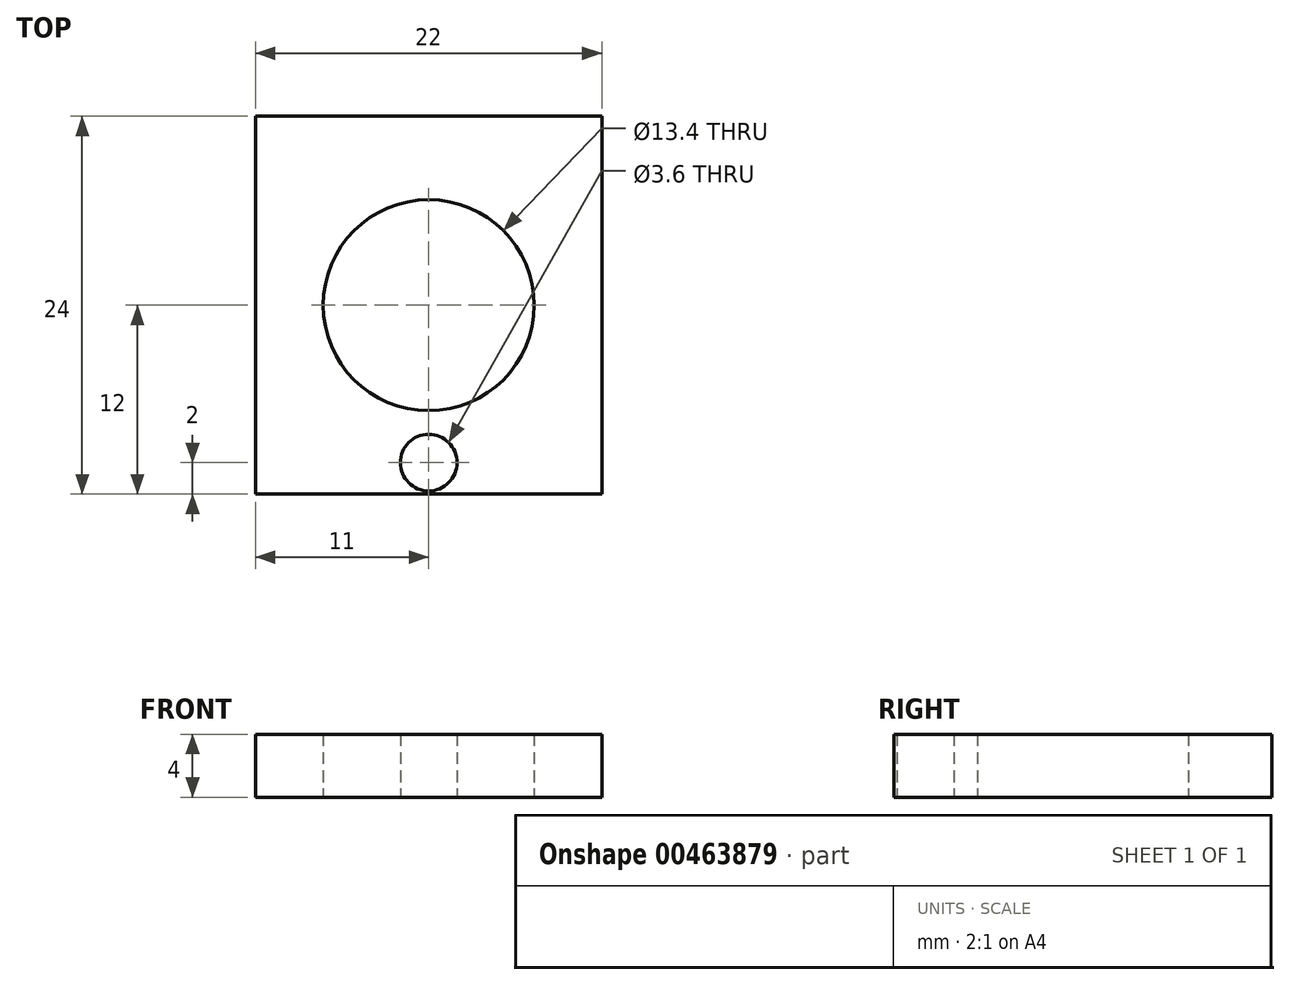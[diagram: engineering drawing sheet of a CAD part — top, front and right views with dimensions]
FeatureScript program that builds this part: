
annotation { "Feature Type Name" : "Feature", "Feature Type Description" : "" }
export const myFeature = defineFeature(function(context is Context, id is Id, definition is map)
    precondition{}
    {
        {
            var Q0;
            Q0=qCreatedBy(makeId("Top.planeOp"),FACE);
            var sketch = newSketch(context, id + "F0", { "sketchPlane" : qUnion([Q0])});
            skLineSegment(sketch, "E0.bottom", {"start": v(11, -12) * mm, "end": v(-11, -12) * mm});
            skLineSegment(sketch, "E0.top", {"start": v(11, 12) * mm, "end": v(-11, 12) * mm});
            skLineSegment(sketch, "E0.left", {"start": v(11, -12) * mm, "end": v(11, 12) * mm});
            skLineSegment(sketch, "E0.right", {"start": v(-11, -12) * mm, "end": v(-11, 12) * mm});
            skPoint(sketch, "E0.middle", {"position": v(0, 0) * mm});
            skSolve(sketch);
        }
        {
            var Q0;
            Q0=qCreatedBy(makeId("Top.planeOp"),FACE);
            var sketch = newSketch(context, id + "F1", { "sketchPlane" : qUnion([Q0])});
            skPoint(sketch, "E1", {"position": v(0, 0) * mm});
            skSolve(sketch);
        }
        {
            var Q0;
            Q0=qCreatedBy(makeId("Top.planeOp"),FACE);
            var sketch = newSketch(context, id + "F2", { "sketchPlane" : qUnion([Q0])});
            skPoint(sketch, "E2", {"position": v(0, -10) * mm});
            skSolve(sketch);
        }
        {
            var Q0;
            Q0 = qSketchRegion(id + "F0", true);
            extrude(context, id + "F3", {"entities" : qUnion([Q0]), "depth" : 4 * mm});
        }
        {
            var Q0;
            Q0=sQuery(id+"F1.wireOp",VERTEX,"E1");
            var Q1;
            Q1=makeQuery(id+"F3.opExtrude","SWEPT_BODY",BODY,{"disambiguationData":[OSD([sQuery(id+"F0.wireOp",EDGE,"E0.bottom"),sQuery(id+"F0.wireOp",EDGE,"E0.top"),sQuery(id+"F0.wireOp",EDGE,"E0.left"),sQuery(id+"F0.wireOp",EDGE,"E0.right")])]});
            hole(context, id + "F4", {"style" : HoleStyle.SIMPLE, "endStyle" : HoleEndStyle.THROUGH, "oppositeDirection" : true, "holeDiameter" : 13.4 * mm, "isTappedThrough" : true, "tappedDepth" : 12 * mm, "tapClearance" : 3, "locations" : qUnion([Q0]), "scope" : qUnion([Q1])});
        }
        {
            var Q0;
            Q0=sQuery(id+"F2.wireOp",VERTEX,"E2");
            var Q1;
            Q1=makeQuery(id+"F3.opExtrude","SWEPT_BODY",BODY,{"disambiguationData":[OSD([sQuery(id+"F0.wireOp",EDGE,"E0.bottom"),sQuery(id+"F0.wireOp",EDGE,"E0.top"),sQuery(id+"F0.wireOp",EDGE,"E0.left"),sQuery(id+"F0.wireOp",EDGE,"E0.right")])]});
            hole(context, id + "F5", {"style" : HoleStyle.SIMPLE, "endStyle" : HoleEndStyle.THROUGH, "oppositeDirection" : true, "holeDiameter" : 3.6 * mm, "isTappedThrough" : true, "tappedDepth" : 12 * mm, "tapClearance" : 3, "locations" : qUnion([Q0]), "scope" : qUnion([Q1])});
        }
    });
